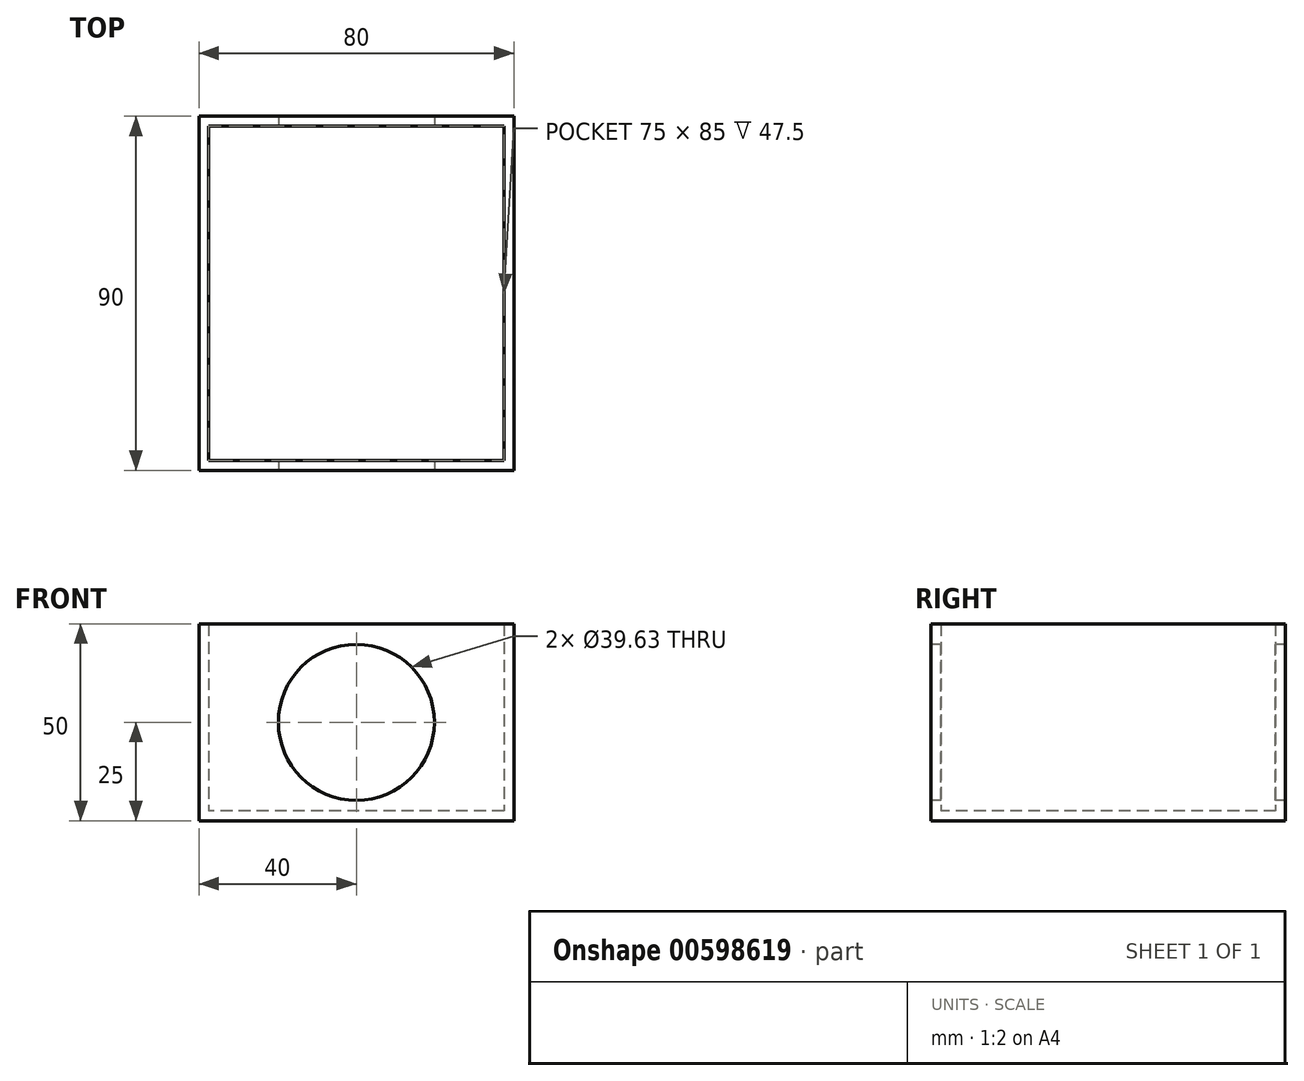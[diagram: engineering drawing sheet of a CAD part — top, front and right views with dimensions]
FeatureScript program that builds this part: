
annotation { "Feature Type Name" : "Feature", "Feature Type Description" : "" }
export const myFeature = defineFeature(function(context is Context, id is Id, definition is map)
    precondition{}
    {
        {
            var Q0;
            Q0=qCreatedBy(makeId("Top.planeOp"),FACE);
            var sketch = newSketch(context, id + "F0", { "sketchPlane" : qUnion([Q0])});
            skLineSegment(sketch, "E0.bottom", {"start": v(40, 45) * mm, "end": v(-40, 45) * mm});
            skLineSegment(sketch, "E0.top", {"start": v(40, -45) * mm, "end": v(-40, -45) * mm});
            skLineSegment(sketch, "E0.left", {"start": v(40, 45) * mm, "end": v(40, -45) * mm});
            skLineSegment(sketch, "E0.right", {"start": v(-40, 45) * mm, "end": v(-40, -45) * mm});
            skPoint(sketch, "E0.middle", {"position": v(0, 0) * mm});
            skSolve(sketch);
        }
        {
            var Q0;
            Q0=makeQuery(id+"F0.imprint","IMPRINT",FACE,{"disambiguationData":[TD([[makeQuery(id+"F0.imprint","IMPRINT",EDGE,{"derivedFrom":sQuery(id+"F0.wireOp",EDGE,"E0.bottom")}),1.0]])]});
            extrude(context, id + "F1", {"entities" : qUnion([Q0]), "depth" : 50 * mm, "offsetDistance" : 25 * mm});
        }
        {
            var Q0;
            Q0=makeQuery(id+"F1.opExtrude","CAP_FACE",FACE,{"disambiguationData":[OSD([sQuery(id+"F0.wireOp",EDGE,"E0.bottom"),sQuery(id+"F0.wireOp",EDGE,"E0.top"),sQuery(id+"F0.wireOp",EDGE,"E0.left"),sQuery(id+"F0.wireOp",EDGE,"E0.right")])],"isStart":false});
            shell(context, id + "F2", {"entities" : qUnion([Q0]), "thickness" : 2.5 * mm});
        }
        {
            var Q0;
            Q0=makeQuery(id+"F1.opExtrude","SWEPT_FACE",FACE,{"disambiguationData":[OSD([sQuery(id+"F0.wireOp",EDGE,"E0.top")])]});
            var sketch = newSketch(context, id + "F3", { "sketchPlane" : qUnion([Q0])});
            skCircle(sketch, "E1", {"center": v(0, 25) * mm, "radius": 19.81 * mm});
            skPoint(sketch, "E1.centerSnap0", {"position": v(40, 25) * mm});
            skPoint(sketch, "E1.centerSnap1", {"position": v(0, 50) * mm});
            skSolve(sketch);
        }
        {
            var Q0;
            Q0=makeQuery(id+"F3.imprint","IMPRINT",FACE,{"disambiguationData":[TD([[makeQuery(id+"F3.imprint","IMPRINT",EDGE,{"derivedFrom":sQuery(id+"F3.wireOp",EDGE,"E1")}),1.0]])]});
            extrude(context, id + "F4", {"entities" : qUnion([Q0]), "operationType" : NewBodyOperationType.REMOVE, "endBound" : BoundingType.THROUGH_ALL, "oppositeDirection" : true, "depth" : 25 * mm, "offsetDistance" : 25 * mm});
        }
    });
